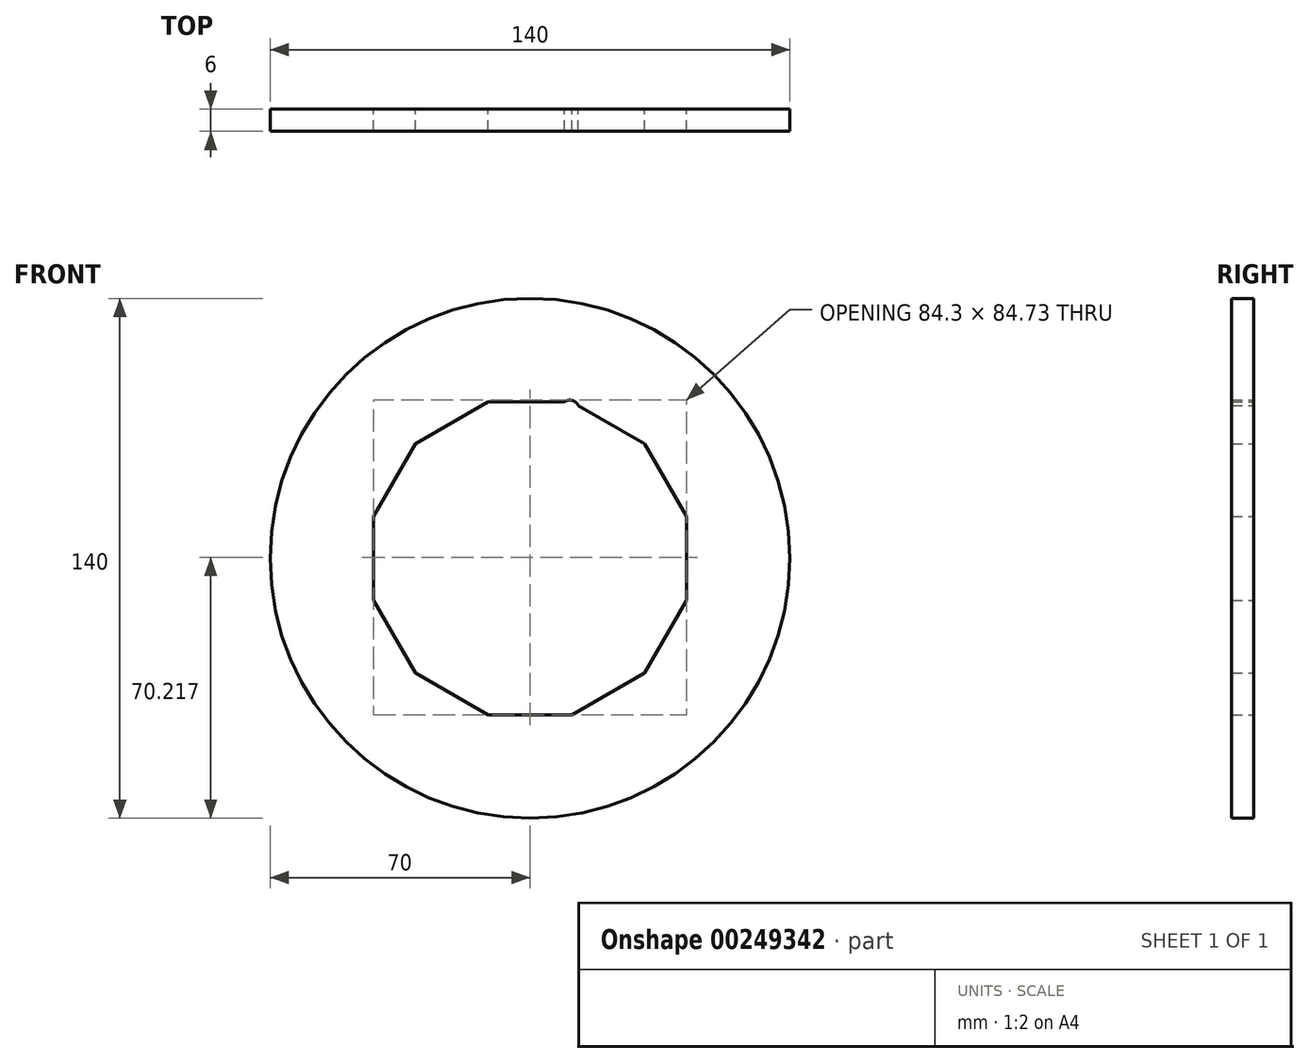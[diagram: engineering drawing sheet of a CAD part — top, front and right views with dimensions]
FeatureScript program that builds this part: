
annotation { "Feature Type Name" : "Feature", "Feature Type Description" : "" }
export const myFeature = defineFeature(function(context is Context, id is Id, definition is map)
    precondition{}
    {
        {
            var Q0;
            Q0=qCreatedBy(makeId("Front.planeOp"),FACE);
            var sketch = newSketch(context, id + "F0", { "sketchPlane" : qUnion([Q0])});
            skCircle(sketch, "E0.cCircle", {"center": v(0, 0) * mm, "radius": 42.15 * mm, "construction": true});
            skLineSegment(sketch, "E0.0", {"start": v(-11.3, 42.15) * mm, "end": v(11.3, 42.15) * mm});
            skLineSegment(sketch, "E0.1", {"start": v(11.3, 42.15) * mm, "end": v(30.86, 30.86) * mm});
            skLineSegment(sketch, "E0.2", {"start": v(30.86, 30.86) * mm, "end": v(42.15, 11.3) * mm});
            skLineSegment(sketch, "E0.3", {"start": v(42.15, 11.3) * mm, "end": v(42.15, -11.3) * mm});
            skLineSegment(sketch, "E0.4", {"start": v(42.15, -11.3) * mm, "end": v(30.86, -30.86) * mm});
            skLineSegment(sketch, "E0.5", {"start": v(30.86, -30.86) * mm, "end": v(11.3, -42.15) * mm});
            skLineSegment(sketch, "E0.6", {"start": v(11.3, -42.15) * mm, "end": v(-11.3, -42.15) * mm});
            skLineSegment(sketch, "E0.7", {"start": v(-11.3, -42.15) * mm, "end": v(-30.86, -30.86) * mm});
            skLineSegment(sketch, "E0.8", {"start": v(-30.86, -30.86) * mm, "end": v(-42.15, -11.3) * mm});
            skLineSegment(sketch, "E0.9", {"start": v(-42.15, -11.3) * mm, "end": v(-42.15, 11.3) * mm});
            skLineSegment(sketch, "E0.10", {"start": v(-42.15, 11.3) * mm, "end": v(-30.86, 30.86) * mm});
            skLineSegment(sketch, "E0.11", {"start": v(-30.86, 30.86) * mm, "end": v(-11.3, 42.15) * mm});
            skPoint(sketch, "E0.0.midPoint", {"position": v(0, 42.15) * mm});
            skCircle(sketch, "E1", {"center": v(0, 0) * mm, "radius": 70 * mm});
            skSolve(sketch);
        }
        {
            var Q0;
            Q0=makeQuery(id+"F0.imprint","IMPRINT",FACE,{"disambiguationData":[TD([[makeQuery(id+"F0.imprint","IMPRINT",EDGE,{"derivedFrom":sQuery(id+"F0.wireOp",EDGE,"E0.0")}),1.0]])]});
            extrude(context, id + "F1", {"entities" : qUnion([Q0]), "depth" : 6 * mm, "symmetric" : true});
        }
        {
            var Q0;
            Q0=qCreatedBy(makeId("Front.planeOp"),FACE);
            var sketch = newSketch(context, id + "F2", { "sketchPlane" : qUnion([Q0])});
            skCircle(sketch, "E2", {"center": v(10.74, 40.09) * mm, "radius": 2.5 * mm});
            skLineSegment(sketch, "E3", {"start": v(10.74, 40.09) * mm, "end": v(0, 0) * mm, "construction": true});
            skSolve(sketch);
        }
        {
            var Q0;
            Q0=makeQuery(id+"F2.imprint","IMPRINT",FACE,{"disambiguationData":[TD([[makeQuery(id+"F2.imprint","IMPRINT",EDGE,{"derivedFrom":sQuery(id+"F2.wireOp",EDGE,"E2")}),1.0]])]});
            extrude(context, id + "F3", {"entities" : qUnion([Q0]), "operationType" : NewBodyOperationType.REMOVE, "depth" : 25 * mm, "symmetric" : true});
        }
    });
